# Revit family: Stool-Soft_Seating-Allermuir-Pause-Mobile-Low-PSS042L
name_source: partatom
category: Furniture
revit_build: Autodesk Revit MEP 2012 (Build: 20110309_2315)
units: mm (PartAtom-declared; Revit-internal decimal feet)

## types (1)
- PSS042L
    04 CSI = 12 51 00
    95 CSI = 12510
    Assembly Code = E2020200
    Brochure URL = http://www.allermuir.net
    CAD Blocks URL = http://www.allermuir.net
    Color Availability = See price list for material options
    Fabric Spec Sheets = http://www.allermuir.net
    LEED Stats URL = http://www.allermuir.net
    Leg Material = Metal - Allermuir - Silver
    Manufacturer = Allermuir
    Manufacturer Fax = (419) 887 5805
    Model = PSS042L
    Overall Depth = 1' - 4 17/32"
    Overall Height = 1' - 7 9/32"
    Overall Width = 1' - 4 17/32"
    Plugin Data URL = http://products.ecoscorecard.com
    Pricing URL = http://www.allermuir.net
    Product Line = Pause
    Product Page URL = http://www.allermuir.net
    Seat Material = Fabric - Allermuir - Silcoates
    Specifications URL = http://www.allermuir.net
    Stacks = No
    Subcategory = Soft Seating
    URL = http://www.allermuir.net
    Weight = 15.0 lb
    Wheel = Plastic - Allermuir - Black
    Wheel Base = Metal - Allermuir - Silver
    ecoScorecard Product Page = http://products.ecoscorecard.com
    ecoScorecard_data = http://thesenatorgroup.ecoscorecard.com

## geometry (parser evidence)
native form markers: Blend x11, Sweep x8
no freeform markers — native parametric forms only
